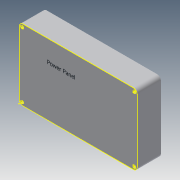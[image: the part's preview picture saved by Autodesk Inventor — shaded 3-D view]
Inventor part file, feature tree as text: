
AUTODESK INVENTOR PART (.ipt)
format: ipt  version: 2014 (Build 180170000, 170)  size: 104,448 bytes
history: native  units: in
note: dims shown in document units (in); Inventor stores cm internally (conversion verified against a paired STEP export)
features: sketch x3, extrude x1, fillet x1, hole x1
ambient origin geometry x8: Origin, YZ Plane, XZ Plane, XY Plane, X Axis, Y Axis, Z Axis, Center Point
bodies: Solid1 (feature_tree)
feature tree (6):
  extrude  "Extrusion1"  Depth=4.5in
  fillet  "Fillet1"  Radius=1.5in
  hole  "Hole1"  [1 undecoded]
  sketch  "Sketch3"  dims[d6=4.125in d7=7.125in d8=0.1875in d9=0.75in d10=0.375in d11=0.25in d12=0.5635in d13=1.0in d14=0.8108in]
  sketch  "Sketch1"  dims[d0=7.5in d1=4.5in d2=1.5in d3=0.0in]
  sketch  "Sketch2"  dims[d4=0.25in d5=7.125in]
note: 1 required parameter value undecoded (feature->parameter linkage not recoverable at this tier; creation-order binding heuristic only, values carry confidence <= 0.55)
